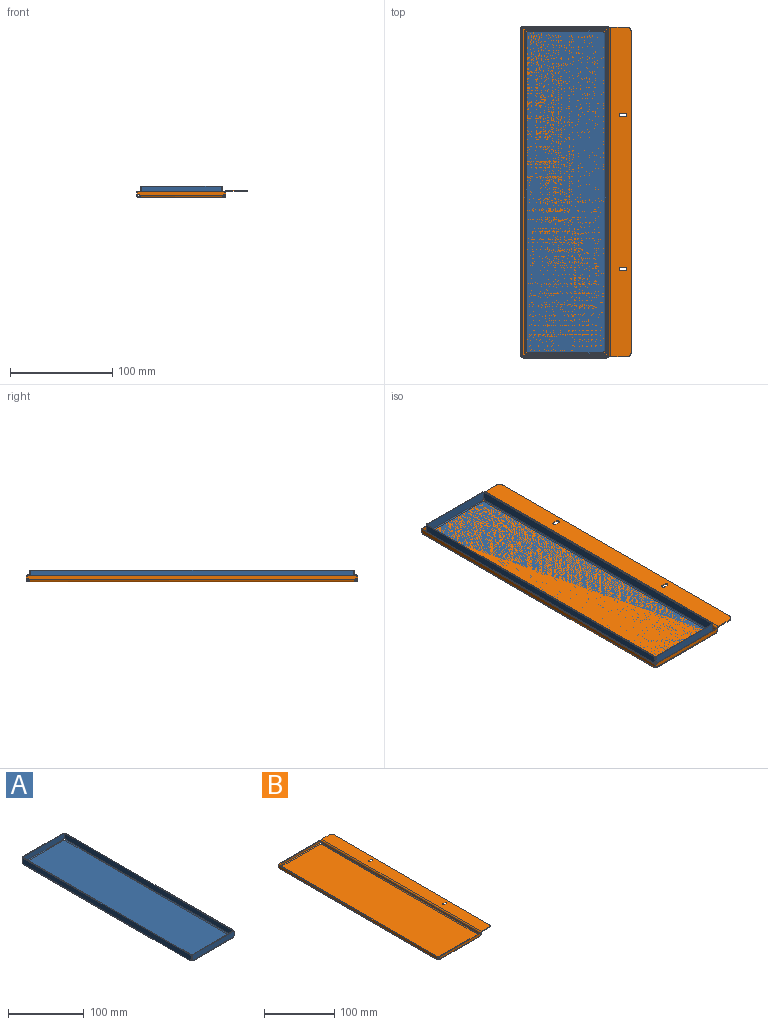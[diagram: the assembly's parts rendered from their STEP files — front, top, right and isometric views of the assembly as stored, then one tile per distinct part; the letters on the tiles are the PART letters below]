
ASSEMBLY  parts=2 mates=1
PART A: 58 faces, bbox 80x317x11 mm
  f0: plane 313x76mm, normal (0,0,-1), area 23785.6mm2, adj f2,f3,f4,f5,f17,f30,f43,f56
  f1: plane 313x76mm, normal (0,0,1), area 23785.6mm2, adj f2,f3,f4,f5,f18,f31,f44,f57
  f2: cylinder r=2.42mm len=1mm, axis (0,0,1), area 1.4mm2, adj f0,f1,f16,f41
  f3: cylinder r=2.42mm len=1mm, axis (0,0,1), area 1.4mm2, adj f0,f1,f29,f42
  f4: cylinder r=2.42mm len=1mm, axis (0,0,1), area 1.4mm2, adj f0,f1,f28,f55
  f5: cylinder r=2.42mm len=1mm, axis (0,0,1), area 1.4mm2, adj f0,f1,f15,f54
  f6: plane 6.73x1mm, normal (1,0,0), area 6.7mm2, adj f8,f10,f12,f13
  f7: plane 6.73x1mm, normal (-1,0,0), area 6.7mm2, adj f8,f10,f11,f14
  f8: plane 77.96x9mm, normal (0,-1,0), area 697.7mm2, adj f6,f7,f9,f11,f12,f13,f14,f17
  f9: plane 75.96x1mm, normal (0,0,1), area 76mm2, adj f8,f10,f11,f12
  f10: plane 77.96x9mm, normal (0,1,0), area 697.7mm2, adj f6,f7,f9,f11,f12,f13,f14,f18
  f11: cylinder r=1mm len=1mm, axis (0,-1,0), area 1.6mm2, adj f7,f8,f9,f10
  f12: cylinder r=1mm len=1mm, axis (0,1,0), area 1.6mm2, adj f6,f8,f9,f10
  f13: cylinder r=2.42mm len=1.97mm, axis (0,1,0), area 2.4mm2, adj f6,f8,f10,f15
  f14: cylinder r=2.42mm len=1.97mm, axis (0,1,0), area 2.4mm2, adj f7,f8,f10,f16
  f15: bspline ~2x2mm, area 2.5mm2, adj f5,f13,f17,f18
  f16: bspline ~2x2mm, area 2.5mm2, adj f2,f14,f17,f18
  f17: cylinder r=2mm len=74.02mm, axis (1,0,0), area 231.3mm2, adj f0,f8,f15,f16
  f18: cylinder r=1mm len=74.02mm, axis (1,0,0), area 115.7mm2, adj f1,f10,f15,f16
  f19: plane 6.73x1mm, normal (1,0,0), area 6.7mm2, adj f22,f23,f25,f27
  f20: plane 6.73x1mm, normal (-1,0,0), area 6.7mm2, adj f22,f23,f24,f26
  f21: plane 75.96x1mm, normal (0,0,1), area 76mm2, adj f22,f23,f24,f25
  f22: plane 77.96x9mm, normal (0,1,0), area 697.7mm2, adj f19,f20,f21,f24,f25,f26,f27,f30
  f23: plane 77.96x9mm, normal (0,-1,0), area 697.7mm2, adj f19,f20,f21,f24,f25,f26,f27,f31
  f24: cylinder r=1mm len=1mm, axis (0,1,0), area 1.6mm2, adj f20,f21,f22,f23
  f25: cylinder r=1mm len=1mm, axis (0,-1,0), area 1.6mm2, adj f19,f21,f22,f23
  f26: cylinder r=2.42mm len=1.97mm, axis (0,-1,0), area 2.4mm2, adj f20,f22,f23,f29
  f27: cylinder r=2.42mm len=1.97mm, axis (0,-1,0), area 2.4mm2, adj f19,f22,f23,f28
  f28: bspline ~2x2mm, area 2.5mm2, adj f4,f27,f30,f31
  f29: bspline ~2x2mm, area 2.5mm2, adj f3,f26,f30,f31
  f30: cylinder r=2mm len=74.02mm, axis (1,0,0), area 231.3mm2, adj f0,f22,f28,f29
  f31: cylinder r=1mm len=74.02mm, axis (1,0,0), area 115.7mm2, adj f1,f23,f28,f29
  f32: plane 6.73x1mm, normal (0,1,0), area 6.7mm2, adj f35,f36,f37,f40
  f33: plane 6.73x1mm, normal (0,-1,0), area 6.7mm2, adj f35,f36,f38,f39
  f34: plane 312.96x1mm, normal (0,0,1), area 313mm2, adj f35,f36,f37,f38
  f35: plane 314.96x9mm, normal (-1,0,0), area 2830.7mm2, adj f32,f33,f34,f37,f38,f39,f40,f43
  f36: plane 314.96x9mm, normal (1,0,0), area 2830.7mm2, adj f32,f33,f34,f37,f38,f39,f40,f44
  f37: cylinder r=1mm len=1mm, axis (-1,0,0), area 1.6mm2, adj f32,f34,f35,f36
  f38: cylinder r=1mm len=1mm, axis (1,0,0), area 1.6mm2, adj f33,f34,f35,f36
  f39: cylinder r=2.42mm len=1.97mm, axis (1,0,0), area 2.4mm2, adj f33,f35,f36,f41
  f40: cylinder r=2.42mm len=1.97mm, axis (1,0,0), area 2.4mm2, adj f32,f35,f36,f42
  f41: bspline ~2x2mm, area 2.5mm2, adj f2,f39,f43,f44
  f42: bspline ~2x2mm, area 2.5mm2, adj f3,f40,f43,f44
  f43: cylinder r=2mm len=311.02mm, axis (0,-1,0), area 975.9mm2, adj f0,f35,f41,f42
  f44: cylinder r=1mm len=311.02mm, axis (0,-1,0), area 487.9mm2, adj f1,f36,f41,f42
  f45: plane 6.73x1mm, normal (0,1,0), area 6.7mm2, adj f47,f49,f51,f52
  f46: plane 6.73x1mm, normal (0,-1,0), area 6.7mm2, adj f47,f49,f50,f53
  f47: plane 314.96x9mm, normal (1,0,0), area 2830.7mm2, adj f45,f46,f48,f50,f51,f52,f53,f56
  f48: plane 312.96x1mm, normal (0,0,1), area 313mm2, adj f47,f49,f50,f51
  f49: plane 314.96x9mm, normal (-1,0,0), area 2830.7mm2, adj f45,f46,f48,f50,f51,f52,f53,f57
  f50: cylinder r=1mm len=1mm, axis (-1,0,0), area 1.6mm2, adj f46,f47,f48,f49
  f51: cylinder r=1mm len=1mm, axis (1,0,0), area 1.6mm2, adj f45,f47,f48,f49
  f52: cylinder r=2.42mm len=1.97mm, axis (-1,0,0), area 2.4mm2, adj f45,f47,f49,f55
  f53: cylinder r=2.42mm len=1.97mm, axis (-1,0,0), area 2.4mm2, adj f46,f47,f49,f54
  f54: bspline ~2x2mm, area 2.5mm2, adj f5,f53,f56,f57
  f55: bspline ~2x2mm, area 2.5mm2, adj f4,f52,f56,f57
  f56: cylinder r=2mm len=311.02mm, axis (0,-1,0), area 975.9mm2, adj f0,f47,f54,f55
  f57: cylinder r=1mm len=311.02mm, axis (0,-1,0), area 487.9mm2, adj f1,f49,f54,f55
PART B: 74 faces, bbox 108x324x7 mm
  f0: plane 320x83mm, normal (0,0,-1), area 26557.6mm2, adj f2,f3,f4,f5,f17,f30,f43,f72
  f1: plane 320x83mm, normal (0,0,1), area 26557.6mm2, adj f2,f3,f4,f5,f18,f31,f44,f73
  f2: cylinder r=2.42mm len=1mm, axis (0,0,1), area 1.4mm2, adj f0,f1,f16,f41
  f3: cylinder r=2.42mm len=1mm, axis (0,0,1), area 1.4mm2, adj f0,f1,f29,f42
  f4: cylinder r=2.42mm len=1mm, axis (0,0,1), area 1.4mm2, adj f0,f1,f28,f71
  f5: cylinder r=2.42mm len=1mm, axis (0,0,1), area 1.4mm2, adj f0,f1,f15,f70
  f6: plane 1.73x1mm, normal (1,0,0), area 1.7mm2, adj f8,f10,f12,f13
  f7: plane 1.73x1mm, normal (-1,0,0), area 1.7mm2, adj f8,f10,f11,f14
  f8: plane 84.96x4mm, normal (0,-1,0), area 335.9mm2, adj f6,f7,f9,f11,f12,f13,f14,f17
  f9: plane 82.96x1mm, normal (0,0,1), area 83mm2, adj f8,f10,f11,f12
  f10: plane 84.96x4mm, normal (0,1,0), area 335.9mm2, adj f6,f7,f9,f11,f12,f13,f14,f18
  f11: cylinder r=1mm len=1mm, axis (0,-1,0), area 1.6mm2, adj f7,f8,f9,f10
  f12: cylinder r=1mm len=1mm, axis (0,1,0), area 1.6mm2, adj f6,f8,f9,f10
  f13: cylinder r=2.42mm len=1.97mm, axis (0,1,0), area 2.4mm2, adj f6,f8,f10,f15
  f14: cylinder r=2.42mm len=1.97mm, axis (0,1,0), area 2.4mm2, adj f7,f8,f10,f16
  f15: bspline ~2x2mm, area 2.5mm2, adj f5,f13,f17,f18
  f16: bspline ~2x2mm, area 2.5mm2, adj f2,f14,f17,f18
  f17: cylinder r=2mm len=81.02mm, axis (1,0,0), area 253.3mm2, adj f0,f8,f15,f16
  f18: cylinder r=1mm len=81.02mm, axis (1,0,0), area 126.7mm2, adj f1,f10,f15,f16
  f19: plane 1.73x1mm, normal (1,0,0), area 1.7mm2, adj f22,f23,f25,f27
  f20: plane 1.73x1mm, normal (-1,0,0), area 1.7mm2, adj f22,f23,f24,f26
  f21: plane 82.96x1mm, normal (0,0,1), area 83mm2, adj f22,f23,f24,f25
  f22: plane 84.96x4mm, normal (0,1,0), area 335.9mm2, adj f19,f20,f21,f24,f25,f26,f27,f30
  f23: plane 84.96x4mm, normal (0,-1,0), area 335.9mm2, adj f19,f20,f21,f24,f25,f26,f27,f31
  f24: cylinder r=1mm len=1mm, axis (0,1,0), area 1.6mm2, adj f20,f21,f22,f23
  f25: cylinder r=1mm len=1mm, axis (0,-1,0), area 1.6mm2, adj f19,f21,f22,f23
  f26: cylinder r=2.42mm len=1.97mm, axis (0,-1,0), area 2.4mm2, adj f20,f22,f23,f29
  f27: cylinder r=2.42mm len=1.97mm, axis (0,-1,0), area 2.4mm2, adj f19,f22,f23,f28
  f28: bspline ~2x2mm, area 2.5mm2, adj f4,f27,f30,f31
  f29: bspline ~2x2mm, area 2.5mm2, adj f3,f26,f30,f31
  f30: cylinder r=2mm len=81.02mm, axis (1,0,0), area 253.3mm2, adj f0,f22,f28,f29
  f31: cylinder r=1mm len=81.02mm, axis (1,0,0), area 126.7mm2, adj f1,f23,f28,f29
  f32: plane 1.73x1mm, normal (0,1,0), area 1.7mm2, adj f35,f36,f37,f40
  f33: plane 1.73x1mm, normal (0,-1,0), area 1.7mm2, adj f35,f36,f38,f39
  f34: plane 319.96x1mm, normal (0,0,1), area 320mm2, adj f35,f36,f37,f38
  f35: plane 321.96x4mm, normal (-1,0,0), area 1283.9mm2, adj f32,f33,f34,f37,f38,f39,f40,f43
  f36: plane 321.96x4mm, normal (1,0,0), area 1283.9mm2, adj f32,f33,f34,f37,f38,f39,f40,f44
  f37: cylinder r=1mm len=1mm, axis (-1,0,0), area 1.6mm2, adj f32,f34,f35,f36
  f38: cylinder r=1mm len=1mm, axis (1,0,0), area 1.6mm2, adj f33,f34,f35,f36
  f39: cylinder r=2.42mm len=1.97mm, axis (1,0,0), area 2.4mm2, adj f33,f35,f36,f41
  f40: cylinder r=2.42mm len=1.97mm, axis (1,0,0), area 2.4mm2, adj f32,f35,f36,f42
  f41: bspline ~2x2mm, area 2.5mm2, adj f2,f39,f43,f44
  f42: bspline ~2x2mm, area 2.5mm2, adj f3,f40,f43,f44
  f43: cylinder r=2mm len=318.02mm, axis (0,-1,0), area 997.9mm2, adj f0,f35,f41,f42
  f44: cylinder r=1mm len=318.02mm, axis (0,-1,0), area 498.9mm2, adj f1,f36,f41,f42
  f45: plane 1.73x1mm, normal (0,1,0), area 1.7mm2, adj f47,f48,f49,f67
  f46: plane 1.73x1mm, normal (0,-1,0), area 1.7mm2, adj f47,f48,f50,f66
  f47: plane 321.96x3mm, normal (1,0,0), area 962.4mm2, adj f45,f46,f49,f50,f69,f72
  f48: plane 321.96x3mm, normal (-1,0,0), area 962.4mm2, adj f45,f46,f49,f50,f68,f73
  f49: cylinder r=2.42mm len=1.97mm, axis (-1,0,0), area 2.4mm2, adj f45,f47,f48,f71
  f50: cylinder r=2.42mm len=1.97mm, axis (-1,0,0), area 2.4mm2, adj f46,f47,f48,f70
  f51: cylinder r=1.6mm len=3.2mm, axis (0,0,-1), area 5mm2, adj f52,f61,f62,f63
  f52: plane 4x1mm, normal (0,1,0), area 4mm2, adj f51,f53,f62,f63
  f53: cylinder r=1.6mm len=3.2mm, axis (0,0,-1), area 5mm2, adj f52,f61,f62,f63
  f54: cylinder r=1.6mm len=3.2mm, axis (0,0,-1), area 5mm2, adj f55,f60,f62,f63
  f55: plane 4x1mm, normal (0,1,0), area 4mm2, adj f54,f56,f62,f63
  f56: cylinder r=1.6mm len=3.2mm, axis (0,0,-1), area 5mm2, adj f55,f60,f62,f63
  f57: plane 311.96x1mm, normal (1,0,0), area 312mm2, adj f62,f63,f64,f65
  f58: plane 15x1mm, normal (0,-1,0), area 15mm2, adj f62,f63,f64,f66
  f59: plane 15x1mm, normal (0,1,0), area 15mm2, adj f62,f63,f65,f67
  f60: plane 4x1mm, normal (0,-1,0), area 4mm2, adj f54,f56,f62,f63
  f61: plane 4x1mm, normal (0,-1,0), area 4mm2, adj f51,f53,f62,f63
  f62: plane 321.96x20mm, normal (0,0,-1), area 6386.8mm2, adj f51,f52,f53,f54,f55,f56,f57,f58
  f63: plane 321.96x20mm, normal (0,0,1), area 6386.8mm2, adj f51,f52,f53,f54,f55,f56,f57,f58
  f64: cylinder r=5mm len=5mm, axis (0,0,-1), area 7.9mm2, adj f57,f58,f62,f63
  f65: cylinder r=5mm len=5mm, axis (0,0,-1), area 7.9mm2, adj f57,f59,f62,f63
  f66: plane 2x2mm, normal (0,-1,0), area 2.4mm2, adj f46,f58,f68,f69
  f67: plane 2x2mm, normal (0,1,0), area 2.4mm2, adj f45,f59,f68,f69
  f68: cylinder r=2mm len=321.96mm, axis (0,-1,0), area 1011.5mm2, adj f48,f63,f66,f67
  f69: cylinder r=1mm len=321.96mm, axis (0,-1,0), area 505.7mm2, adj f47,f62,f66,f67
  f70: bspline ~2x2mm, area 2.5mm2, adj f5,f50,f72,f73
  f71: bspline ~2x2mm, area 2.5mm2, adj f4,f49,f72,f73
  f72: cylinder r=2mm len=318.02mm, axis (0,-1,0), area 997.9mm2, adj f0,f47,f70,f71
  f73: cylinder r=1mm len=318.02mm, axis (0,-1,0), area 498.9mm2, adj f1,f48,f70,f71
PLACE A t=(0,-157.5,0)mm
PLACE B t=(0,-161,0)mm
MATE slider A.f1 <-> B.f1  axis (0,0,1) through (0,0,0)mm
